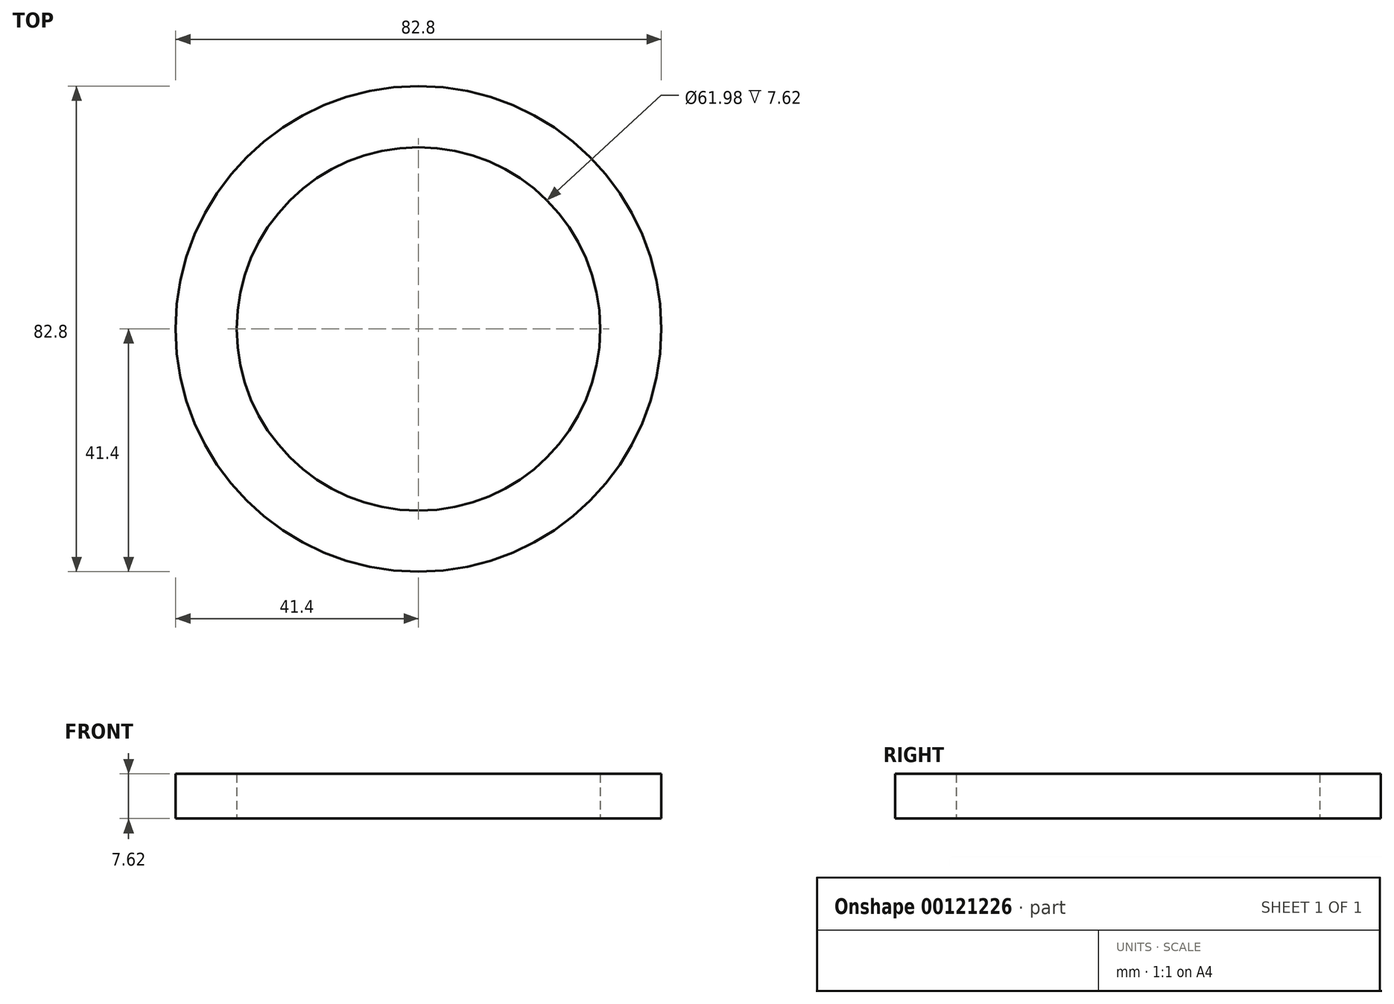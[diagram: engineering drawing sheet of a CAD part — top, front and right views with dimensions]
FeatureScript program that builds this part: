
annotation { "Feature Type Name" : "Feature", "Feature Type Description" : "" }
export const myFeature = defineFeature(function(context is Context, id is Id, definition is map)
    precondition{}
    {
        {
            var Q0;
            Q0=qCreatedBy(makeId("Top.planeOp"),FACE);
            var sketch = newSketch(context, id + "F0", { "sketchPlane" : qUnion([Q0])});
            skCircle(sketch, "E0", {"center": v(0, 0) * mm, "radius": 41.4 * mm});
            skCircle(sketch, "E1", {"center": v(0, 0) * mm, "radius": 30.99 * mm});
            skSolve(sketch);
        }
        {
            var Q0;
            Q0=makeQuery(id+"F0.imprint","IMPRINT",FACE,{"disambiguationData":[TD([[makeQuery(id+"F0.imprint","IMPRINT",EDGE,{"derivedFrom":sQuery(id+"F0.wireOp",EDGE,"E0")}),1.0]])]});
            extrude(context, id + "F1", {"entities" : qUnion([Q0]), "depth" : 7.62 * mm});
        }
    });
